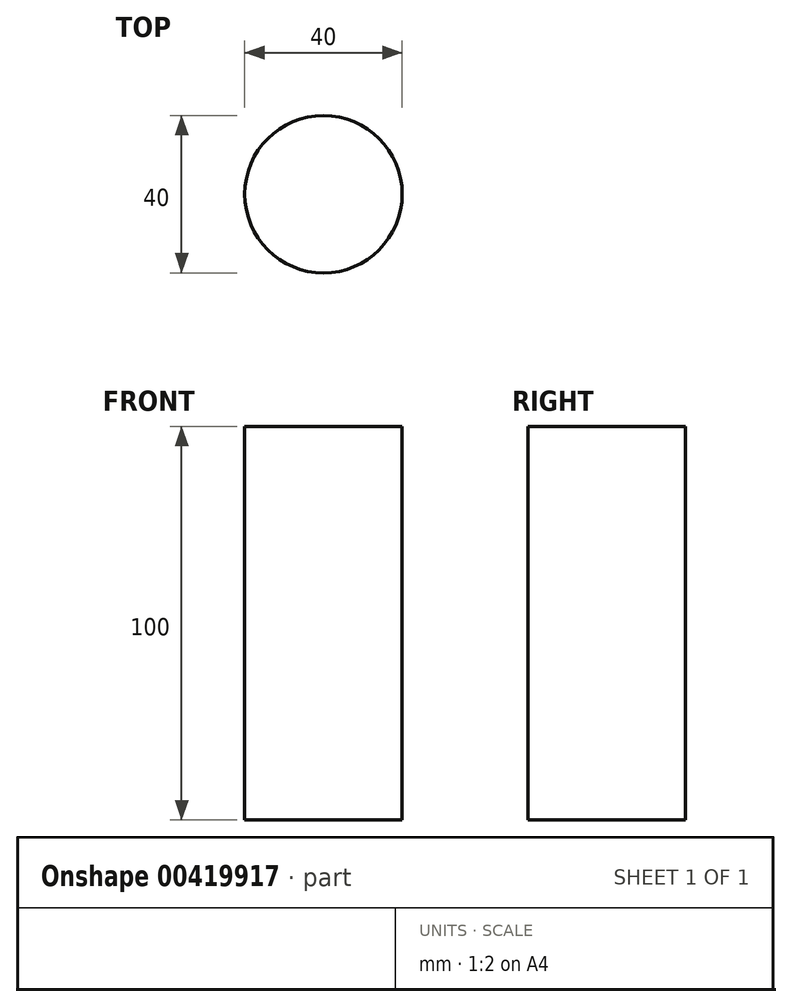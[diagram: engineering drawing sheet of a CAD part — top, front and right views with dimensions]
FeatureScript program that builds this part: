
annotation { "Feature Type Name" : "Feature", "Feature Type Description" : "" }
export const myFeature = defineFeature(function(context is Context, id is Id, definition is map)
    precondition{}
    {
        {
            var Q0;
            Q0=qCreatedBy(makeId("Top.planeOp"),FACE);
            var sketch = newSketch(context, id + "F0", { "sketchPlane" : qUnion([Q0])});
            skCircle(sketch, "E0", {"center": v(0, 0) * mm, "radius": 20 * mm});
            skSolve(sketch);
        }
        {
            var Q0;
            Q0 = qSketchRegion(id + "F0", true);
            extrude(context, id + "F1", {"entities" : qUnion([Q0]), "flatOperationType" : FlatOperationType.REMOVE, "depth" : 100 * mm, "offsetDistance" : 25 * mm, "domain" : OperationDomain.MODEL});
        }
    });
